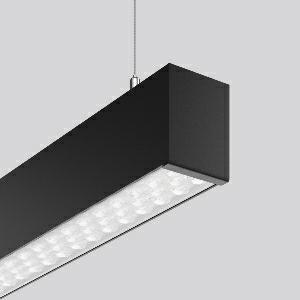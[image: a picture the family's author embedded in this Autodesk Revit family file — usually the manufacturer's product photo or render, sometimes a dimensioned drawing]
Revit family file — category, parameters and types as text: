
# Revit family: linedo_single_ip20_312564_003_243b
name_source: partatom
category: Lighting Fixtures
units: mm (PartAtom-declared; Revit-internal decimal feet)

## family parameters
Cut with Voids When Loaded = No
Host = Face
Light Source = No
Part Type = Normal
Room Calculation Point = No
Round Connector Dimension = Use Diameter
Shared = No

## types (1)
- LINEDO single IP20 (1 x LED Modul 830, 6100 lm, 3000)
    Apparent Load = 40 VA
    CIE Flux Codes = 86 96 99 100 100
    Color Rendering = 80
    Color Temperature = 3000
    Default Elevation = 1800 mm
    Description = Series: LINEDO single IP20
Stylish pendant luminaire. Housing: extruded aluminium profile, powder-coated. End cap aluminium powder-coated, without visible screws. High-efficiency LED units with optimum light control thanks to clear plastic (PC) lens optics. 2-point steel cable suspension freely positionable and infinitely height-adjustable. With power cord (2.5 m). Please order canopy separately if required. Perfect for office areas (RUG < 19) and environments with computer screens in accordance with EN 12464-1. 
Colour: deep black, matt (RAL 9005)
Length: 2264 mm
Width: 58 mm
Height: 76 mm
Suspension length: 100-1500 mm
Lamp: LED
Socket: without socket
Colour temperature: 3000K
Colour rendering index (CRI): 80
System power: 40 W
Rated luminous flux: 6100 lm
Beam angle Down: 59°
Luminous efficiency: 153 lm/W
Control gear: Regulated power supply
Protection class: I
Type of protection: IP 20
    Height = 76 mm
    Lamp = 1 x LED Modul 830
    Lamp Light Flux = 6100 lm
    Lamp count = 1
    Length = 2264 mm
    Lifetime = 50000 h
    Luminous efficacy = 153 lm/W
    Manufacturer = RZB
    ModVariant = No
    Model = 312564.003
    Mounting Place = Ceiling
    Mounting Type = Surface mounted, Pendant
    Number of Poles = 1
    OnlyDefault = Yes
    Power Factor = 1
    Product Name = LINEDO single IP20
    Product group = Pendant luminaires
    ProductGroupID = 902
    Protection Class = Protection class I
    Protection Degree = IP 20
    RLX_Detail_Level = 1
    RLX_Emergency_Light_Flux = 0 lm
    RLX_Emergency_Type = 0
    RLX_Emergency_Type_DB = No
    RlxData = <blob elided: 34997 chars, md5=971b0b62>
    Socket = socket
    Standby Power = 0 W
    System Light Flux = 6100 lm
    System Power = 40 W
    Type Comments = ALEA SPOT
    Type Image = 312563.003.jpg
    URL = http://relux.com
    VarID = ---
    Voltage = 230 V
    Voltage Range = 220-240 V
    Weight = 0.00 kg
    Width = 58 mm

## geometry (parser evidence)
native form markers: Blend x4, Sweep x10
no freeform markers — native parametric forms only
